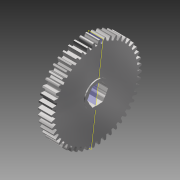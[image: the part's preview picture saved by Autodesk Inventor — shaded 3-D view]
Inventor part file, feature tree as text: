
AUTODESK INVENTOR PART (.ipt)
format: ipt  version: 2016 SP1 (Build 200210100, 210)  size: 400,384 bytes
history: native  units: in
note: dims shown in document units (in); Inventor stores cm internally (conversion verified against a paired STEP export)
features: plane x1, other x1
ambient origin geometry x8: Origin, YZ Plane, XZ Plane, XY Plane, X Axis, Y Axis, Z Axis, Center Point
bodies: Solid1 (feature_tree)
feature tree (2):
  plane  "Work Plane2"
  other  "Bore"
